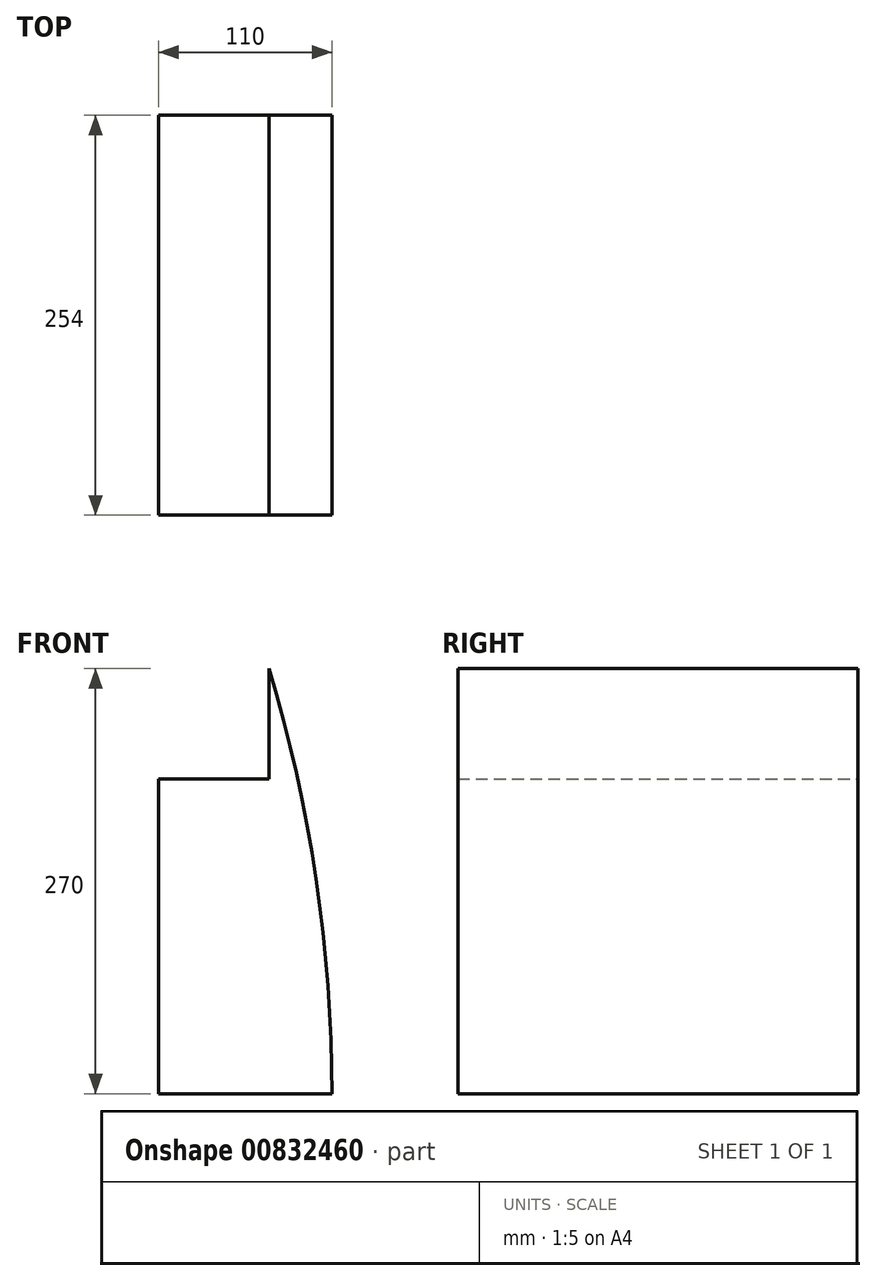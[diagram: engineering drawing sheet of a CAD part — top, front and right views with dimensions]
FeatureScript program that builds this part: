
annotation { "Feature Type Name" : "Feature", "Feature Type Description" : "" }
export const myFeature = defineFeature(function(context is Context, id is Id, definition is map)
    precondition{}
    {
        {
            var Q0;
            Q0=qCreatedBy(makeId("Front.planeOp"),FACE);
            var sketch = newSketch(context, id + "F0", { "sketchPlane" : qUnion([Q0])});
            skLineSegment(sketch, "E0", {"start": v(0, 0) * mm, "end": v(110, 0) * mm});
            skLineSegment(sketch, "E1", {"start": v(0, 0) * mm, "end": v(0, 200) * mm});
            skLineSegment(sketch, "E2", {"start": v(0, 200) * mm, "end": v(70, 200) * mm});
            skLineSegment(sketch, "E3", {"start": v(70, 200) * mm, "end": v(70, 270) * mm});
            skArc(sketch, "E4", {"start": v(110, 0) * mm, "mid": v(99.95, 136.47) * mm, "end": v(70, 270) * mm});
            skSolve(sketch);
        }
        {
            var Q0;
            Q0 = qSketchRegion(id + "F0", true);
            extrude(context, id + "F1", {"entities" : qUnion([Q0]), "depth" : 254 * mm, "offsetDistance" : 25 * mm});
        }
    });
